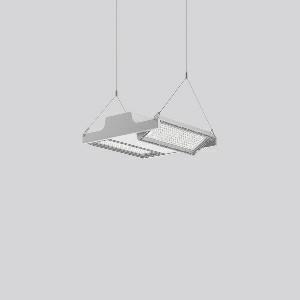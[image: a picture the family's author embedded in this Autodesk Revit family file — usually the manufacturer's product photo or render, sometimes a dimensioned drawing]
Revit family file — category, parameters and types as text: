
# Revit family: light_case_921680_004_1_76_51d2
name_source: partatom
category: Lighting Fixtures
units: mm (PartAtom-declared; Revit-internal decimal feet)

## family parameters
Cut with Voids When Loaded = No
Host = Face
Light Source = No
Part Type = Normal
Room Calculation Point = No
Round Connector Dimension = Use Diameter
Shared = No

## types (1)
- LIGHT CASE (1 x LED Modul 865, 8650 lm, 6500)
    Apparent Load = 117 VA
    CIE Flux Codes = 88 95 99 100 100
    Color Rendering = 80
    Color Temperature = 6500
    Default Elevation = 1800 mm
    Description = Series: LIGHT CASE
Flat highbay luminaire for chain or cable suspension with 2 LED modules that can be swivelled. Housing: die cast aluminium and sheet steel, powder-coated. Optimised thermal management thanks to special luminaire design. Self-cleaning heat sink for constant heat dissipation. Cover: plastic (polycarbonate, shockproof), with integrated four-row lens system. LED modules can be swivelled ± 30° for optimum illumination. Suitable for chain or steel cable suspension (to be provided on site). With 5-pin connection terminal (1.5 m). With integrated movement sensor and light sensor for daylight detection on request. Ball impact proof in accordance with DIN 18032-03 (except steel cable suspension). Luminaire with limited surface temperature in accordance with EN 60598-2-24 for use in environments in which a deposit of conductive dust on the luminaire can be expected. 
Colour: silver, matt (approx. RAL 9006)
Length: 406 mm
Width: 397 mm
Height: 110 mm
Lamp: LED
Socket: without socket
Colour temperature: 6500K
Colour rendering index (CRI): 80
System power: 117 W
Rated luminous flux: 17300 lm
Luminous efficiency: 148 lm/W
Control gear: Converter, dimmable, DALI
Protection class: I
Type of protection: IP 65
    Height = 110 mm
    Lamp = 1 x LED Modul 865
    Lamp Light Flux = 8650 lm
    Lamp count = 1
    Length = 406 mm
    Lifetime = 50000 h
    Luminous efficacy = 148 lm/W
    Manufacturer = RZB
    ModVariant = No
    Model = 921680.004.1.76
    Mounting Place = Ceiling
    Mounting Type = Pendant
    Number of Poles = 1
    OnlyDefault = Yes
    Power Factor = 1
    Product Name = LIGHT CASE
    Product group = Pendant commercial luminaires
    ProductGroupID = 903
    Protection Class = Protection class I
    Protection Degree = IP 65
    RLX_Detail_Level = 1
    RLX_Emergency_Light_Flux = 0 lm
    RLX_Emergency_Type = 0
    RLX_Emergency_Type_DB = No
    RlxData = <blob elided: 26413 chars, md5=0749035e>
    Socket = socket
    Standby Power = 0 W
    System Light Flux = 17300 lm
    System Power = 117 W
    Type Comments = Product without accessories
    Type Image = 921517.004.76.jpg
    URL = http://relux.com
    VarID = ---
    Voltage = 230 V
    Voltage Range = 220-240 V
    Weight = 0.00 kg
    Width = 397 mm

## geometry (parser evidence)
native form markers: Blend x4, Sweep x16
no freeform markers — native parametric forms only
